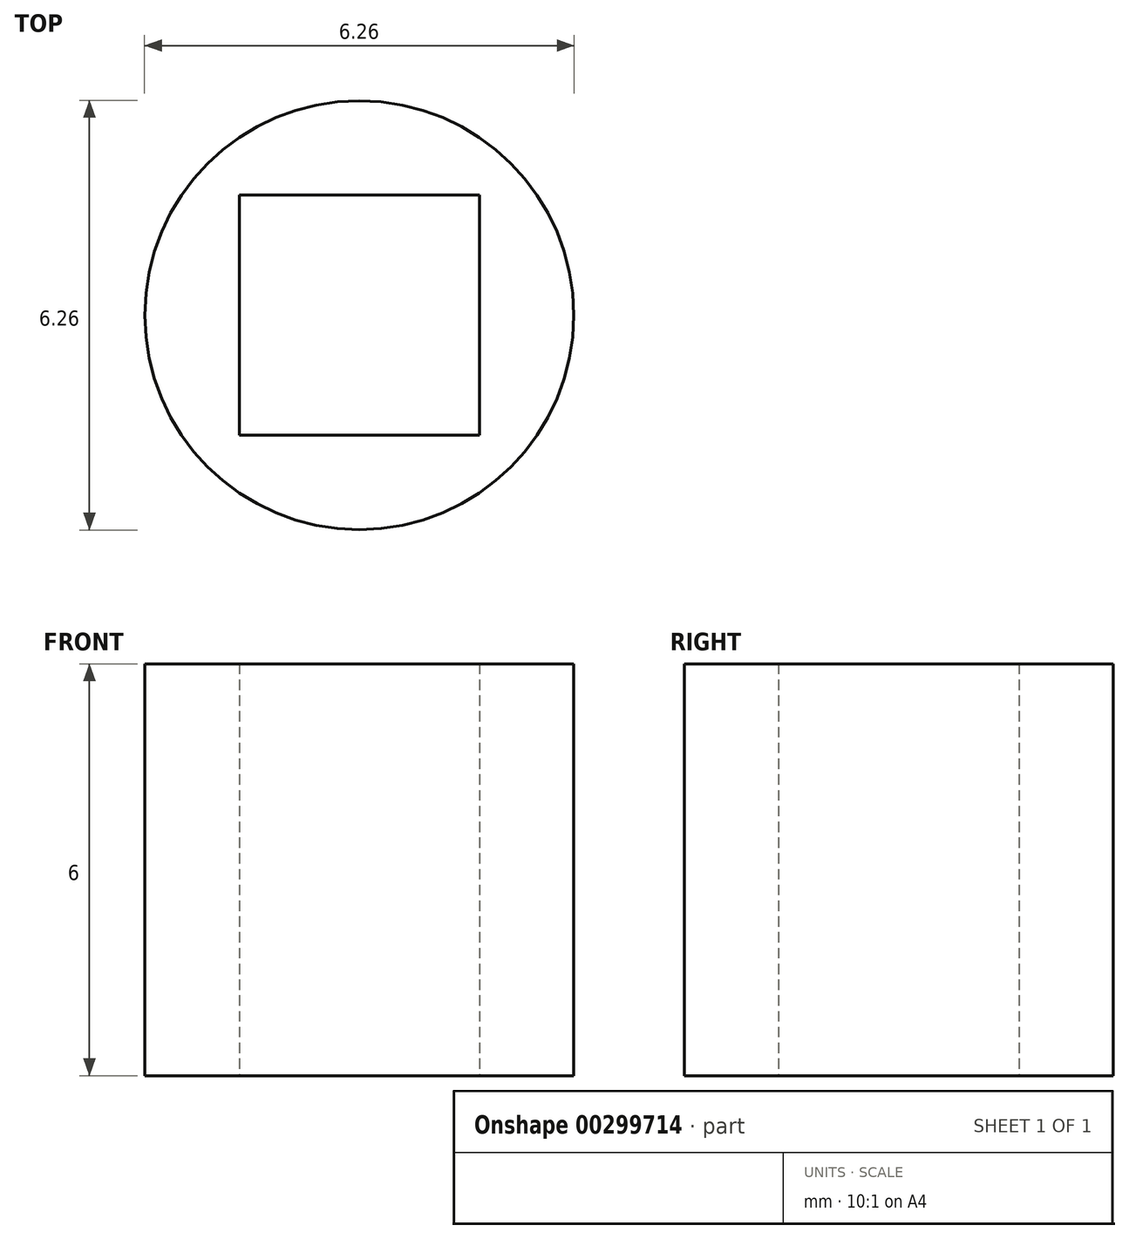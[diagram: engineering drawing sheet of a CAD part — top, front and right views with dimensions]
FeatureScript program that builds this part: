
annotation { "Feature Type Name" : "Feature", "Feature Type Description" : "" }
export const myFeature = defineFeature(function(context is Context, id is Id, definition is map)
    precondition{}
    {
        {
            var Q0;
            Q0=qCreatedBy(makeId("Top.planeOp"),FACE);
            var sketch = newSketch(context, id + "F0", { "sketchPlane" : qUnion([Q0])});
            skCircle(sketch, "E0", {"center": v(0, 0) * mm, "radius": 3.12 * mm});
            skLineSegment(sketch, "E1.bottom", {"start": v(-1.75, -1.75) * mm, "end": v(1.75, -1.75) * mm});
            skLineSegment(sketch, "E1.top", {"start": v(-1.75, 1.75) * mm, "end": v(1.75, 1.75) * mm});
            skLineSegment(sketch, "E1.left", {"start": v(-1.75, -1.75) * mm, "end": v(-1.75, 1.75) * mm});
            skLineSegment(sketch, "E1.right", {"start": v(1.75, -1.75) * mm, "end": v(1.75, 1.75) * mm});
            skSolve(sketch);
        }
        {
            var Q0;
            Q0=makeQuery(id+"F0.imprint","IMPRINT",FACE,{"disambiguationData":[TD([[makeQuery(id+"F0.imprint","IMPRINT",EDGE,{"derivedFrom":sQuery(id+"F0.wireOp",EDGE,"E0")}),1.0]])]});
            extrude(context, id + "F1", {"entities" : qUnion([Q0]), "depth" : 6 * mm});
        }
    });
